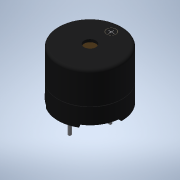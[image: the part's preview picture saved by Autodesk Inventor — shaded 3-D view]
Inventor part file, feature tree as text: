
AUTODESK INVENTOR PART (.ipt)
format: ipt  version: 2021.3 (Build 253353000, 353)  size: 214,528 bytes
history: native  units: mm
features: extrude x10, sketch x10, plane x2, fillet x1, pattern_circular x1, chamfer x1, projected_geometry x1
ambient origin geometry x8: Origin, YZ Plane, XZ Plane, XY Plane, X Axis, Y Axis, Z Axis, Center Point
bodies: Solid1 (feature_tree)
feature tree (26):
  extrude  "Extrusion1"  Depth=9.5mm TaperAngle=0.0deg
  plane  "Work Plane1"
  extrude  "Extrusion2"  Depth=8.5mm
  extrude  "Extrusion3"  Depth=1.0mm
  extrude  "Extrusion4"  Depth=0.5mm
  fillet  "Fillet1"  Radius=0.5mm
  extrude  "Extrusion5"  Depth=0.5mm TaperAngle=0.0deg
  pattern_circular  "Circular Pattern1"  Count=3 Angle=360.0deg
  extrude  "Extrusion6"  Depth=3.8mm
  extrude  "Extrusion7"  Depth=6.0mm
  chamfer  "Chamfer1"  Distance=4.0mm
  extrude  "Extrusion8"  Depth=0.1mm TaperAngle=0.0deg
  extrude  "Extrusion9"  [1 undecoded]
  plane  "Work Plane2"
  extrude  "Extrusion10"  Depth=11.5mm
  sketch  "Sketch1"  dims[d0=12.0mm d1=9.5mm d2=0.0mm]
  sketch  "Sketch2"  dims[d3=-0.5mm d4=8.5mm]
  projected_geometry  "Projected Loop1"
  sketch  "Sketch3"  dims[d5=1.0mm d6=0.0mm d7=2.2mm]
  sketch  "Sketch4"  dims[d8=0.5mm d9=0.0mm d10=10.5mm d11=0.5mm d12=0.0mm]
  sketch  "Sketch5"  dims[d13=0.5mm d14=0.5mm d15=0.0mm d16=30.0mm d17=360.0deg]
  sketch  "Sketch6"  dims[d19=0.6mm d20=3.8mm]
  sketch  "Sketch7"  dims[d21=6.0mm d22=0.0mm d23=0.6mm]
  sketch  "Sketch8"  dims[d24=3.8mm d25=4.0mm d26=0.0mm]
  sketch  "Sketch9"  dims[d27=0.2mm d28=2.0mm d29=45.0deg d30=0.1mm d31=0.0mm]
  sketch  "Sketch10"  dims[d32=0.01mm d33=0.0mm d34=-6.0mm d35=11.5mm d36=0.1mm d37=0.0mm]
note: 1 required parameter value undecoded (feature->parameter linkage not recoverable at this tier; creation-order binding heuristic only, values carry confidence <= 0.55)
